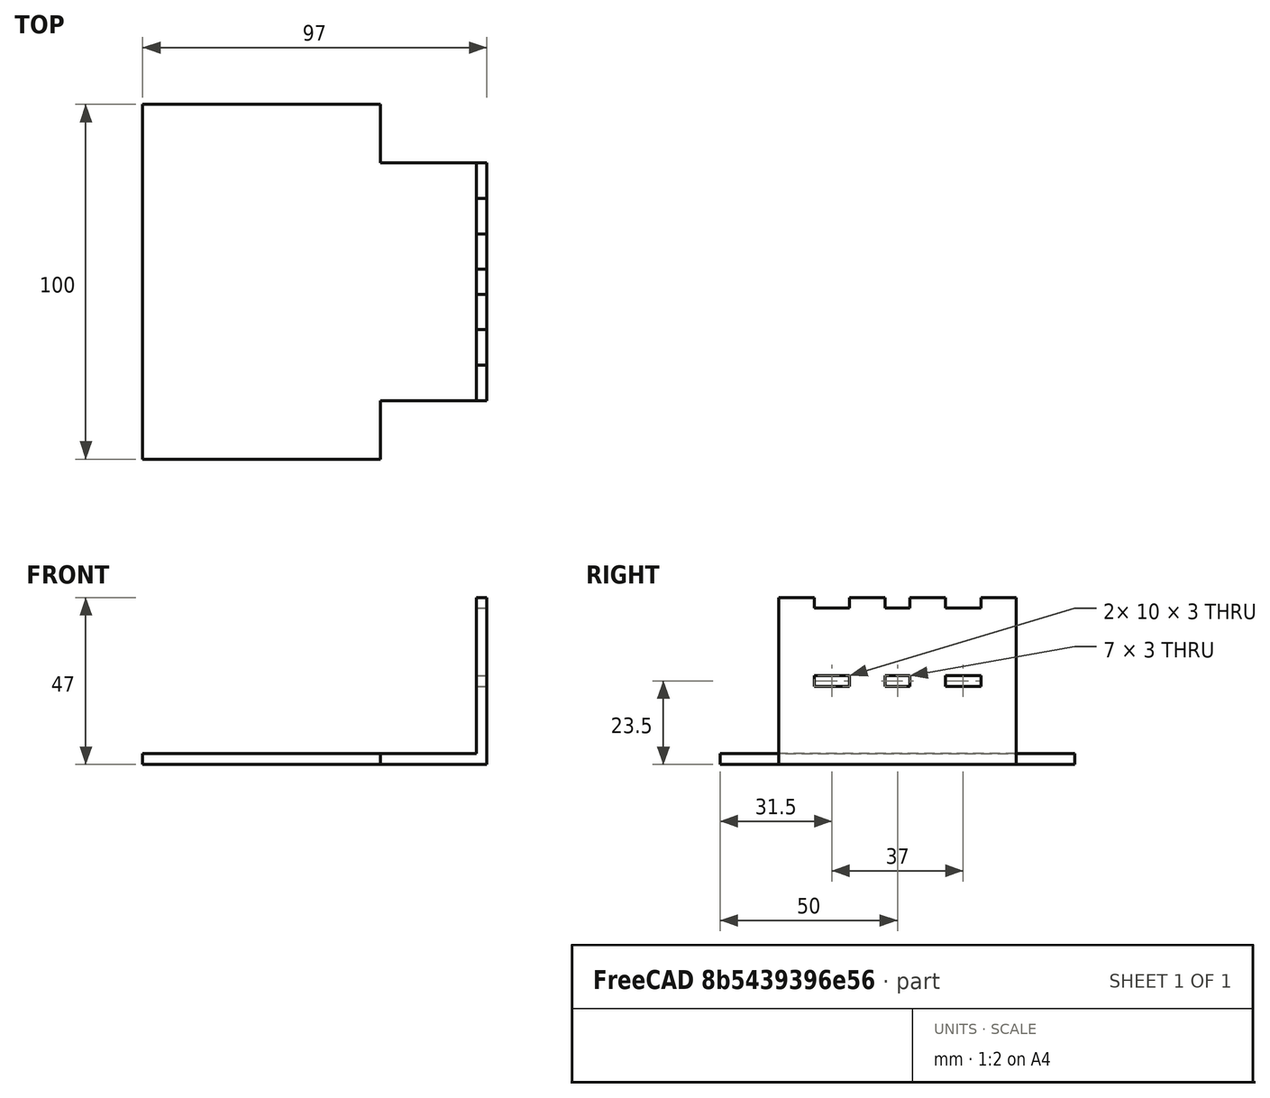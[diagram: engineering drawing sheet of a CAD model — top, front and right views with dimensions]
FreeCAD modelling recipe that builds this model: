
FCSTD DOCUMENT  (FreeCAD 0.16R6706 (Git))
Label: base mas tapa atras
License: All rights reserved
LicenseURL: http://en.wikipedia.org/wiki/All_rights_reserved
objects: Part::Box×10, Part::Cut×8, Part::MultiFuse×1
note: 19 computed .brp shape members not serialized (recipe doc carries the construction recipe); baked Part::Feature solids carry a one-line shape summary decoded from their .brp

FEATURE [Part::Box] Box  label="base"
  Height = 3
  Length = 97
  Width = 100
FEATURE [Part::Box] Box001  label="agujeros ruedas"
  Height = 3
  Length = 30
  Placement = pos=(67,0,0) rot=(0,0,1;0rad)
  Width = 16.5
FEATURE [Part::Cut] Cut
  Base = -> Box
  Tool = -> Box001
FEATURE [Part::Box] Box002  label="agujeros ruedas001"
  Height = 11
  Length = 30
  Placement = pos=(67,83.5,-4) rot=(0,0,1;0rad)
  Width = 16.5
FEATURE [Part::Cut] Cut001  label="base con agujeros rueda"
  Base = -> Cut
  Tool = -> Box002
FEATURE [Part::Box] Box003  label="tapa atras"
  Height = 47
  Length = 3
  Placement = pos=(94,16.5,0) rot=(0,0,1;0rad)
  Width = 67
FEATURE [Part::Box] Box005  label="2"
  Height = 3
  Length = 9
  Placement = pos=(91,26.5,44) rot=(0,0,1;0rad)
  Width = 10
FEATURE [Part::Box] Box008  label="5"
  Height = 3
  Length = 9
  Placement = pos=(91,63.5,44) rot=(0,0,1;0rad)
  Width = 10
FEATURE [Part::Box] Box010  label="centro"
  Height = 3
  Length = 9
  Placement = pos=(91,46.5,44) rot=(0,0,1;0rad)
  Width = 7
FEATURE [Part::Cut] Cut002
  Base = -> Box003
  Tool = -> Box005
FEATURE [Part::Cut] Cut003
  Base = -> Cut002
  Tool = -> Box010
FEATURE [Part::Cut] Cut004  label="tapa atras con almenas"
  Base = -> Cut003
  Tool = -> Box008
FEATURE [Part::Box] Box026  label="2001001"
  Height = 3
  Length = 9
  Placement = pos=(94,26.5,22) rot=(0,0,1;0rad)
  Width = 10
FEATURE [Part::Box] Box027  label="centro002"
  Height = 3
  Length = 9
  Placement = pos=(94,46.5,22) rot=(0,0,1;0rad)
  Width = 7
FEATURE [Part::Box] Box028  label="5001001"
  Height = 3
  Length = 9
  Placement = pos=(94,63.5,22) rot=(0,0,1;0rad)
  Width = 10
FEATURE [Part::Cut] Cut015
  Base = -> Cut004
  Tool = -> Box026
FEATURE [Part::Cut] Cut016
  Base = -> Cut015
  Tool = -> Box027
FEATURE [Part::Cut] Cut017  label="tapa atras cabada"
  Base = -> Cut016
  Tool = -> Box028
FEATURE [Part::MultiFuse] Fusion004  label="base mas tapa atras acabado"
  Shapes = -> [Cut017,Cut001]
